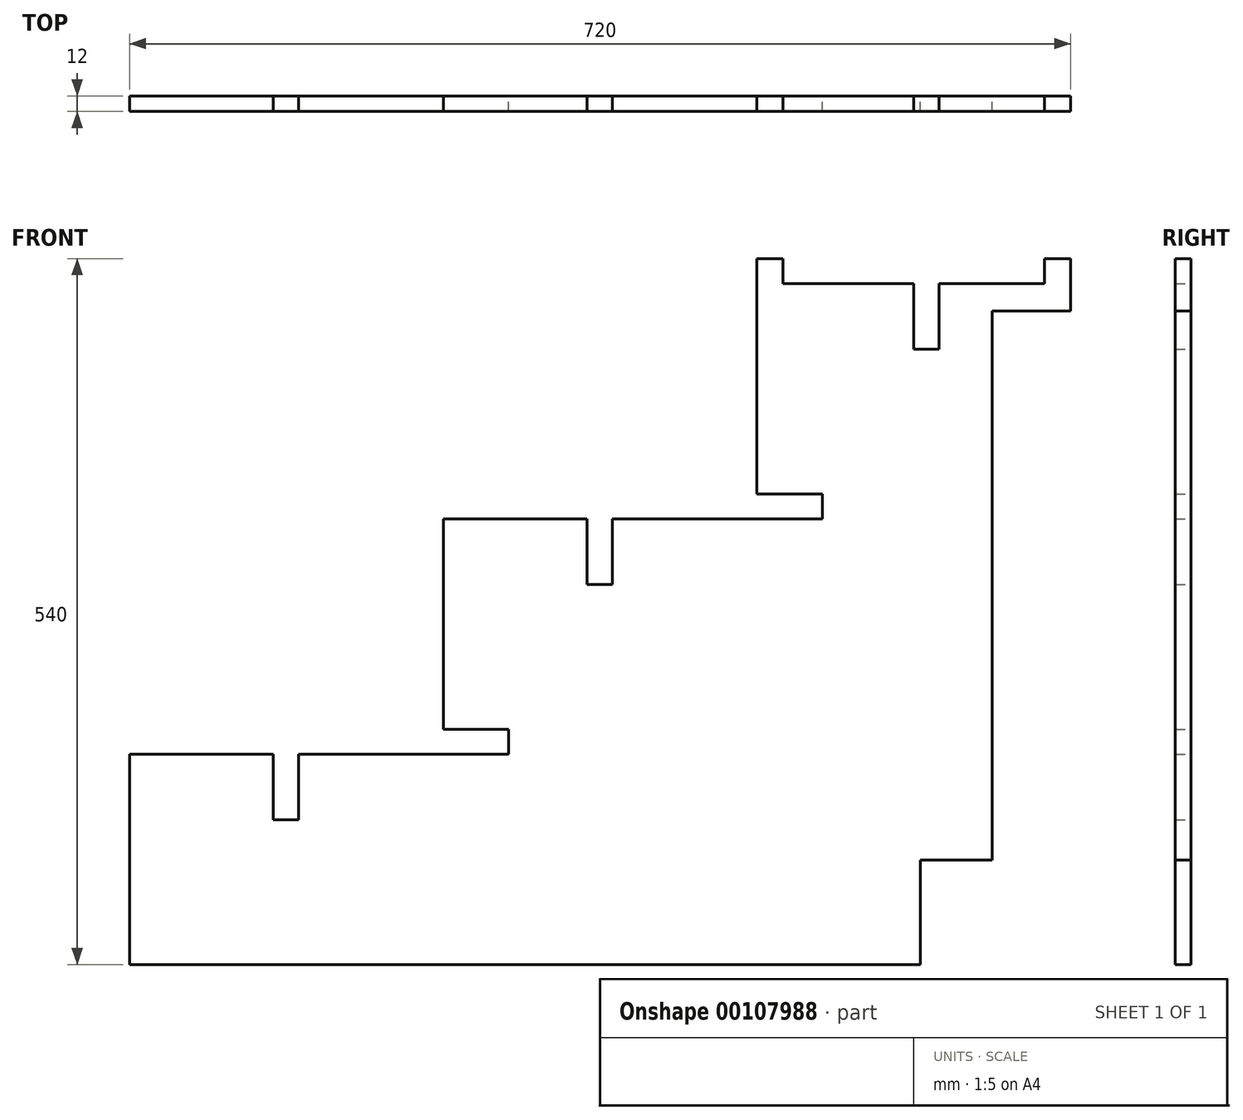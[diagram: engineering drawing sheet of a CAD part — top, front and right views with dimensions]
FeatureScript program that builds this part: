
annotation { "Feature Type Name" : "Feature", "Feature Type Description" : "" }
export const myFeature = defineFeature(function(context is Context, id is Id, definition is map)
    precondition{}
    {
        {
            var Q0;
            Q0=qCreatedBy(makeId("Front.planeOp"),FACE);
            var sketch = newSketch(context, id + "F0", { "sketchPlane" : qUnion([Q0])});
            skLineSegment(sketch, "E0", {"start": v(-395.13, -240.3) * mm, "end": v(-395.13, -79.5) * mm});
            skLineSegment(sketch, "E1", {"start": v(-395.13, -79.5) * mm, "end": v(-285.13, -79.5) * mm});
            skLineSegment(sketch, "E2", {"start": v(-172.84, -79.5) * mm, "end": v(-105.13, -79.5) * mm});
            skLineSegment(sketch, "E3", {"start": v(-105.13, -79.5) * mm, "end": v(-105.13, -60.3) * mm});
            skLineSegment(sketch, "E4", {"start": v(-105.13, -60.3) * mm, "end": v(-155.13, -60.3) * mm});
            skLineSegment(sketch, "E5", {"start": v(-155.13, -60.3) * mm, "end": v(-155.13, 100.5) * mm});
            skLineSegment(sketch, "E6", {"start": v(-155.13, 100.5) * mm, "end": v(-45.13, 100.5) * mm});
            skLineSegment(sketch, "E7", {"start": v(134.87, 100.5) * mm, "end": v(134.87, 119.7) * mm});
            skLineSegment(sketch, "E8", {"start": v(134.87, 119.7) * mm, "end": v(84.87, 119.7) * mm});
            skLineSegment(sketch, "E9", {"start": v(84.87, 119.7) * mm, "end": v(84.87, 299.7) * mm});
            skLineSegment(sketch, "E10", {"start": v(84.87, 299.7) * mm, "end": v(104.87, 299.7) * mm});
            skLineSegment(sketch, "E11", {"start": v(104.87, 299.7) * mm, "end": v(104.87, 280.5) * mm});
            skLineSegment(sketch, "E12", {"start": v(104.87, 280.5) * mm, "end": v(204.87, 280.5) * mm});
            skLineSegment(sketch, "E13", {"start": v(304.87, 280.5) * mm, "end": v(304.87, 299.7) * mm});
            skLineSegment(sketch, "E14", {"start": v(304.87, 299.7) * mm, "end": v(324.87, 299.7) * mm});
            skLineSegment(sketch, "E15", {"start": v(324.87, 299.7) * mm, "end": v(324.87, 259.7) * mm});
            skLineSegment(sketch, "E16", {"start": v(324.87, 259.7) * mm, "end": v(264.87, 259.7) * mm});
            skLineSegment(sketch, "E17", {"start": v(264.87, 259.7) * mm, "end": v(264.87, -160.3) * mm});
            skLineSegment(sketch, "E18", {"start": v(209.87, -240.3) * mm, "end": v(-395.13, -240.3) * mm});
            skLineSegment(sketch, "E19.top", {"start": v(-285.13, -129.5) * mm, "end": v(-265.93, -129.5) * mm});
            skLineSegment(sketch, "E19.left", {"start": v(-285.13, -79.5) * mm, "end": v(-285.13, -129.5) * mm});
            skLineSegment(sketch, "E19.right", {"start": v(-265.93, -79.5) * mm, "end": v(-265.93, -129.5) * mm});
            skLineSegment(sketch, "E20.trimOffspring", {"start": v(-265.93, -79.5) * mm, "end": v(-172.84, -79.5) * mm});
            skLineSegment(sketch, "E21.top", {"start": v(204.87, 230.5) * mm, "end": v(224.07, 230.5) * mm});
            skLineSegment(sketch, "E21.left", {"start": v(204.87, 280.5) * mm, "end": v(204.87, 230.5) * mm});
            skLineSegment(sketch, "E21.right", {"start": v(224.07, 280.5) * mm, "end": v(224.07, 230.5) * mm});
            skLineSegment(sketch, "E22.trimOffspring", {"start": v(224.07, 280.5) * mm, "end": v(304.87, 280.5) * mm});
            skLineSegment(sketch, "E23.top", {"start": v(-45.13, 50.5) * mm, "end": v(-25.93, 50.5) * mm});
            skLineSegment(sketch, "E23.left", {"start": v(-45.13, 100.5) * mm, "end": v(-45.13, 50.5) * mm});
            skLineSegment(sketch, "E23.right", {"start": v(-25.93, 100.5) * mm, "end": v(-25.93, 50.5) * mm});
            skLineSegment(sketch, "E24.trimOffspring", {"start": v(-25.93, 100.5) * mm, "end": v(134.87, 100.5) * mm});
            skLineSegment(sketch, "E25.bottom", {"start": v(209.87, -160.3) * mm, "end": v(264.87, -160.3) * mm});
            skLineSegment(sketch, "E25.left", {"start": v(209.87, -160.3) * mm, "end": v(209.87, -240.3) * mm});
            skSolve(sketch);
        }
        {
            var Q0;
            Q0=makeQuery(id+"F0.imprint","IMPRINT",FACE,{"disambiguationData":[TD([[makeQuery(id+"F0.imprint","IMPRINT",EDGE,{"derivedFrom":sQuery(id+"F0.wireOp",EDGE,"E0")}),-1.0]])]});
            extrude(context, id + "F1", {"entities" : qUnion([Q0]), "endBound" : BoundingType.SYMMETRIC, "depth" : 12 * mm});
        }
    });
